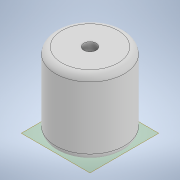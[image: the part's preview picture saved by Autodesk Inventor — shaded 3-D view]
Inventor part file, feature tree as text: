
AUTODESK INVENTOR PART (.ipt)
format: ipt  version: 2020 (Build 240168000, 168)  size: 131,584 bytes
history: native  units: in
note: dims shown in document units (in); Inventor stores cm internally (conversion verified against a paired STEP export)
features: extrude x2, sketch x2, plane x1, fillet x1
ambient origin geometry x8: Origin, YZ Plane, XZ Plane, XY Plane, X Axis, Y Axis, Z Axis, Center Point
bodies: Solid1 (feature_tree)
feature tree (6):
  extrude  "Extrusion1"  Depth=0.9449in TaperAngle=0.0deg
  plane  "Work Plane1"
  extrude  "Extrusion2"  Depth=0.0787in TaperAngle=0.0deg
  fillet  "Fillet2"  Radius=0.0787in
  sketch  "Sketch1"  dims[d0=0.8661in d1=0.9449in d2=0.0in]
  sketch  "Sketch2"  dims[d6=0.1575in d7=1.2992in d8=0.0in d10=0.0787in d3=0.0197in d4=0.0344in]
